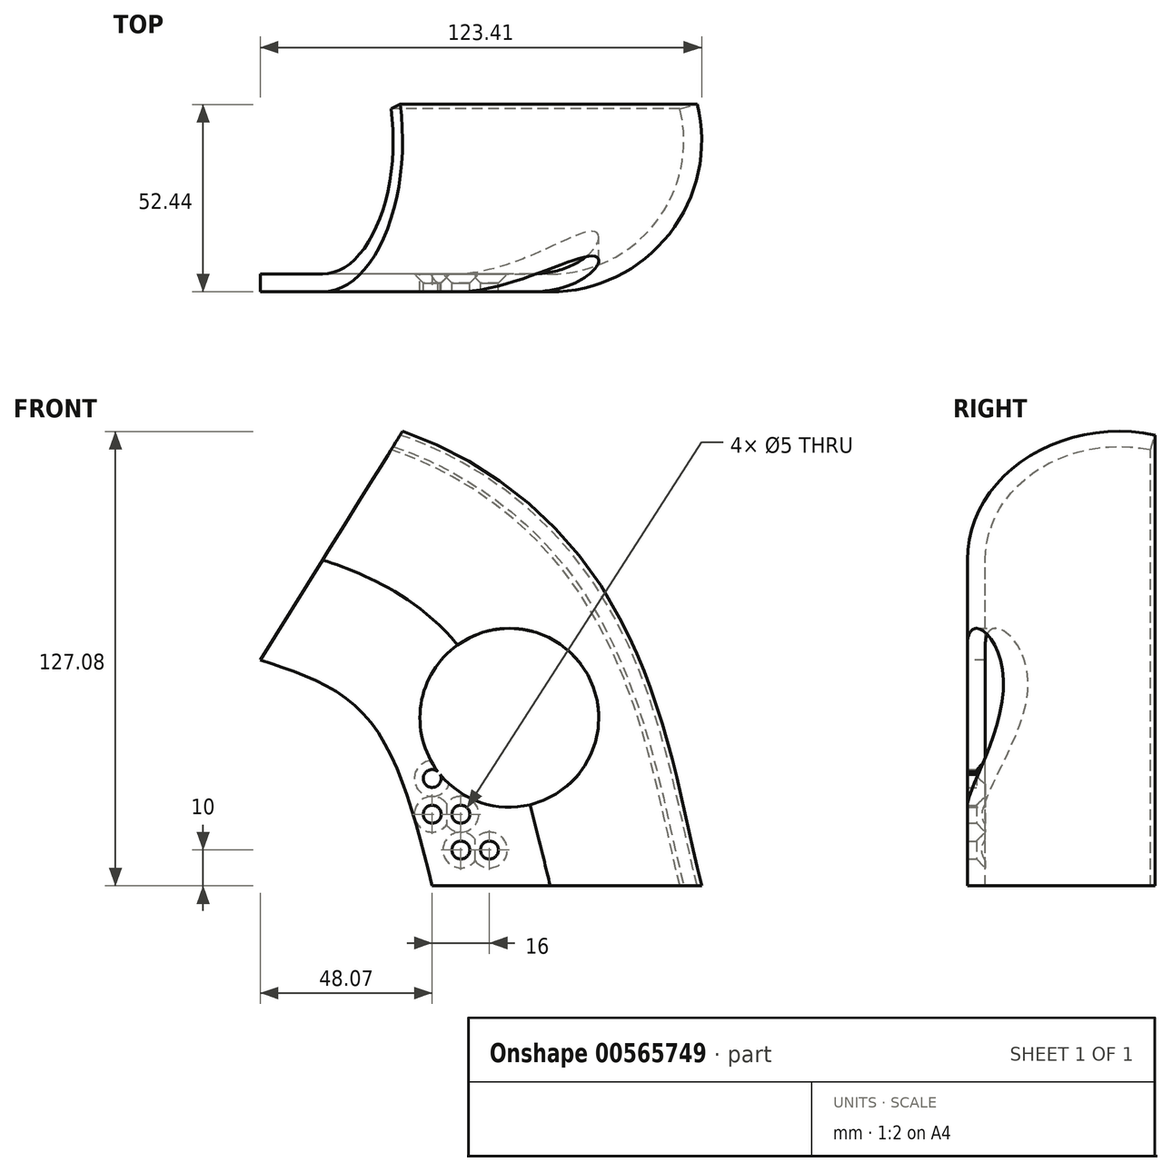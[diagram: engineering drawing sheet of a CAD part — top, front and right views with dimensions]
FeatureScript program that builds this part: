
annotation { "Feature Type Name" : "Feature", "Feature Type Description" : "" }
export const myFeature = defineFeature(function(context is Context, id is Id, definition is map)
    precondition{}
    {
        {
            var Q0;
            Q0=qCreatedBy(makeId("Top.planeOp"),FACE);
            var sketch = newSketch(context, id + "F0", { "sketchPlane" : qUnion([Q0])});
            skLineSegment(sketch, "E0", {"start": v(0, 0) * mm, "end": v(33, 0) * mm});
            skArc(sketch, "E1", {"start": v(33, 0) * mm, "mid": v(62.39, 14.3) * mm, "end": v(69.26, 46.25) * mm});
            skArc(sketch, "E2.0", {"start": v(33, -5) * mm, "mid": v(66.32, 11.22) * mm, "end": v(74.11, 47.44) * mm});
            skLineSegment(sketch, "E3.0", {"start": v(0, -5) * mm, "end": v(33, -5) * mm});
            skLineSegment(sketch, "E4", {"start": v(0, 0) * mm, "end": v(0, -5) * mm});
            skLineSegment(sketch, "E5", {"start": v(69.26, 46.25) * mm, "end": v(74.11, 47.44) * mm});
            skSolve(sketch);
        }
        {
            var Q0;
            Q0=qCreatedBy(makeId("Front.planeOp"),FACE);
            var sketch = newSketch(context, id + "F1", { "sketchPlane" : qUnion([Q0])});
            skFitSpline(sketch, "E6", {"points": [v(0, 0) * mm, v(-18.7, 47.53) * mm, v(-48.07, 63.1) * mm], "startDerivative": vector(-24.94, 99.98) * mm, "endDerivative": vector(-72.92, 23.5) * mm});
            skSolve(sketch);
        }
        {
            var Q0;
            Q0=makeQuery(id+"F0.imprint","IMPRINT",FACE,{"disambiguationData":[TD([[makeQuery(id+"F0.imprint","IMPRINT",EDGE,{"derivedFrom":sQuery(id+"F0.wireOp",EDGE,"E0")}),-1.0]])]});
            var Q1;
            Q1=sQuery(id+"F1.wireOp",EDGE,"E6");
            sweep(context, id + "F2", {"profiles" : qUnion([Q0]), "path" : qUnion([Q1])});
        }
        {
            var Q0;
            Q0=qCreatedBy(makeId("Front.planeOp"),FACE);
            var sketch = newSketch(context, id + "F3", { "sketchPlane" : qUnion([Q0])});
            skCircle(sketch, "E7", {"center": v(-39.27, 2.98) * mm, "radius": 25 * mm});
            skSolve(sketch);
        }
        {
            var Q0;
            Q0=makeQuery(id+"F3.imprint","IMPRINT",FACE,{"disambiguationData":[TD([[makeQuery(id+"F3.imprint","IMPRINT",EDGE,{"derivedFrom":sQuery(id+"F3.wireOp",EDGE,"E7")}),1.0]])]});
            extrude(context, id + "F4", {"entities" : qUnion([Q0]), "endBound" : BoundingType.SYMMETRIC, "depth" : 25 * mm, "offsetDistance" : 25 * mm});
        }
        {
            var Q0;
            Q0=makeQuery(id+"F4.opExtrude","SWEPT_BODY",BODY,{"disambiguationData":[OSD([sQuery(id+"F3.wireOp",EDGE,"E7")])]});
            transform(context, id + "F5", {"entities" : qUnion([Q0]), "transformType" : TransformType.TRANSLATION_3D, "dx" : 60.83 * mm, "dy" : 0 * mm, "dz" : 44 * mm, "makeCopy" : false});
        }
        {
            var Q0;
            Q0=makeQuery(id+"F4.opExtrude","SWEPT_BODY",BODY,{"disambiguationData":[OSD([sQuery(id+"F3.wireOp",EDGE,"E7")])]});
            var Q1;
            Q1=makeQuery(id+"F2.opSweep","SWEPT_BODY",BODY,{"disambiguationData":[OSD([sQuery(id+"F0.wireOp",EDGE,"E0"),sQuery(id+"F0.wireOp",EDGE,"E1"),sQuery(id+"F0.wireOp",EDGE,"E2.0"),sQuery(id+"F0.wireOp",EDGE,"E3.0"),sQuery(id+"F0.wireOp",EDGE,"E4"),sQuery(id+"F0.wireOp",EDGE,"E5"),sQuery(id+"F1.wireOp",EDGE,"E6")])]});
            booleanBodies(context, id + "F6", {"operationType" : BooleanOperationType.SUBTRACTION, "tools" : qUnion([Q0]), "targets" : qUnion([Q1])});
        }
        {
            var Q0;
            Q0=qCreatedBy(makeId("Front.planeOp"),FACE);
            var sketch = newSketch(context, id + "F7", { "sketchPlane" : qUnion([Q0])});
            skLineSegment(sketch, "E8", {"start": v(16, 0) * mm, "end": v(16, 10) * mm});
            skLineSegment(sketch, "E9", {"start": v(16, 10) * mm, "end": v(8, 10) * mm});
            skLineSegment(sketch, "E10", {"start": v(8, 10) * mm, "end": v(8, 20) * mm});
            skLineSegment(sketch, "E11", {"start": v(8, 20) * mm, "end": v(0, 20) * mm});
            skLineSegment(sketch, "E12", {"start": v(0, 20) * mm, "end": v(0, 30) * mm});
            skSolve(sketch);
        }
        {
            var Q0;
            Q0=sQuery(id+"F7.wireOp",VERTEX,"E9.start");
            var Q1;
            Q1=sQuery(id+"F7.wireOp",VERTEX,"E10.start");
            var Q2;
            Q2=sQuery(id+"F7.wireOp",VERTEX,"E11.start");
            var Q3;
            Q3=sQuery(id+"F7.wireOp",VERTEX,"E11.end");
            var Q4;
            Q4=sQuery(id+"F7.wireOp",VERTEX,"E12.end");
            var Q5;
            Q5=makeQuery(id+"F2.opSweep","SWEPT_BODY",BODY,{"disambiguationData":[OSD([sQuery(id+"F0.wireOp",EDGE,"E0"),sQuery(id+"F0.wireOp",EDGE,"E1"),sQuery(id+"F0.wireOp",EDGE,"E2.0"),sQuery(id+"F0.wireOp",EDGE,"E3.0"),sQuery(id+"F0.wireOp",EDGE,"E4"),sQuery(id+"F0.wireOp",EDGE,"E5"),sQuery(id+"F1.wireOp",EDGE,"E6")])]});
            hole(context, id + "F8", {"style" : HoleStyle.C_SINK, "endStyle" : HoleEndStyle.THROUGH, "oppositeDirection" : true, "holeDiameter" : 5 * mm, "cSinkDiameter" : 10 * mm, "cSinkAngle" : 90 * degree, "majorDiameter" : 5 * mm, "isTappedThrough" : true, "tappedDepth" : 12 * mm, "tapClearance" : 3, "startFromSketch" : true, "locations" : qUnion([Q0, Q1, Q2, Q3, Q4]), "scope" : qUnion([Q5])});
        }
    });
